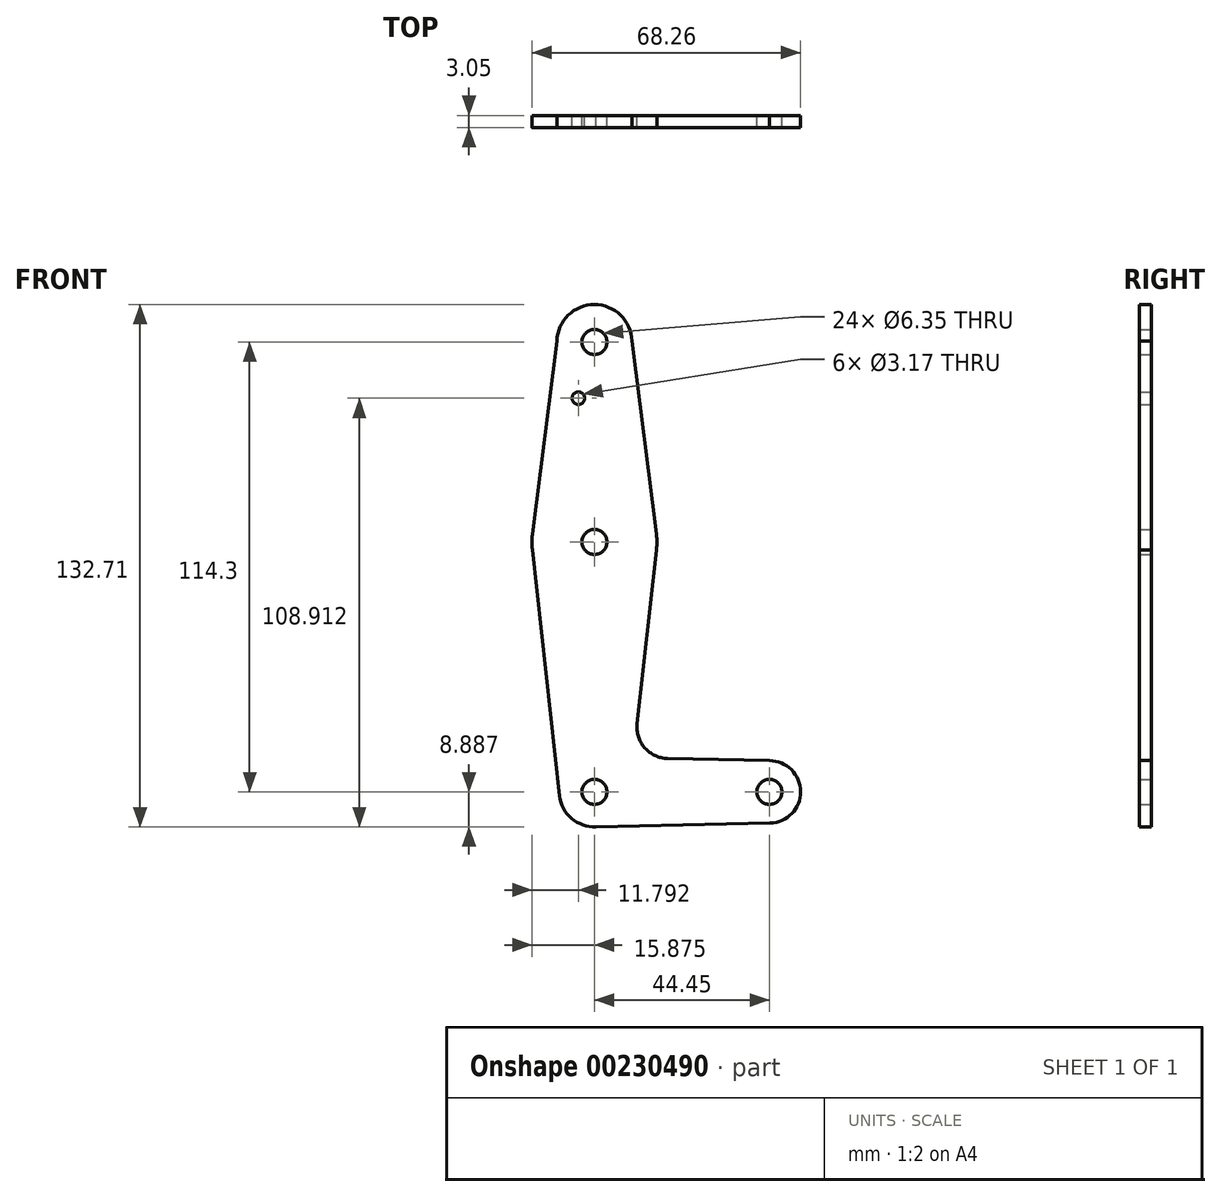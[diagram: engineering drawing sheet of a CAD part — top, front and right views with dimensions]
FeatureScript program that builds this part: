
annotation { "Feature Type Name" : "Feature", "Feature Type Description" : "" }
export const myFeature = defineFeature(function(context is Context, id is Id, definition is map)
    precondition{}
    {
        {
            var Q0;
            Q0=qCreatedBy(makeId("Front.planeOp"),FACE);
            var sketch = newSketch(context, id + "F0", { "sketchPlane" : qUnion([Q0])});
            skLineSegment(sketch, "E0", {"start": v(-39.2, 9.58) * mm, "end": v(-39.2, -53.92) * mm});
            skLineSegment(sketch, "E1", {"start": v(-39.2, -53.92) * mm, "end": v(5.25, -53.92) * mm});
            skCircle(sketch, "E2", {"center": v(-39.2, 60.38) * mm, "radius": 9.53 * mm});
            skCircle(sketch, "E3", {"center": v(-39.2, 9.58) * mm, "radius": 15.88 * mm});
            skCircle(sketch, "E4", {"center": v(-39.2, -53.92) * mm, "radius": 8.89 * mm});
            skLineSegment(sketch, "E5", {"start": v(-39.2, 60.38) * mm, "end": v(-39.2, -53.92) * mm});
            skCircle(sketch, "E6", {"center": v(5.25, -53.92) * mm, "radius": 7.94 * mm});
            skLineSegment(sketch, "E7", {"start": v(-48.73, 60.62) * mm, "end": v(-54.95, 11.58) * mm});
            skLineSegment(sketch, "E8", {"start": v(-29.68, 60.64) * mm, "end": v(-23.46, 11.58) * mm});
            skLineSegment(sketch, "E9", {"start": v(-54.95, 7.58) * mm, "end": v(-48.04, -54.9) * mm});
            skLineSegment(sketch, "E10", {"start": v(-23.46, 7.58) * mm, "end": v(-28.34, -36.6) * mm});
            skLineSegment(sketch, "E11", {"start": v(5.25, -45.99) * mm, "end": v(-20.61, -45.43) * mm});
            skLineSegment(sketch, "E12", {"start": v(-39.2, -62.81) * mm, "end": v(5.42, -61.86) * mm});
            skCircle(sketch, "E13", {"center": v(-39.2, 60.38) * mm, "radius": 3.17 * mm});
            skCircle(sketch, "E14", {"center": v(-39.2, 9.58) * mm, "radius": 3.18 * mm});
            skCircle(sketch, "E15", {"center": v(-43.29, 46.1) * mm, "radius": 1.59 * mm});
            skCircle(sketch, "E16", {"center": v(-39.2, -53.92) * mm, "radius": 3.17 * mm});
            skCircle(sketch, "E17", {"center": v(5.25, -53.92) * mm, "radius": 3.17 * mm});
            skPoint(sketch, "E18.newPointA", {"position": v(-30.37, -54.9) * mm});
            skArc(sketch, "E18.filletArc", {"start": v(-28.34, -36.6) * mm, "mid": v(-26.42, -42.72) * mm, "end": v(-20.61, -45.43) * mm});
            skSolve(sketch);
        }
        {
            var Q0;
            Q0 = qSketchRegion(id + "F0", true);
            var Q1;
            {var subQ0=sQuery(id+"F0.wireOp",EDGE,"E16");var subQ1=sQuery(id+"F0.wireOp",EDGE,"E1");var subQ2=makeQuery(id+"F0.imprint","INTERSECT",VERTEX,{"derivedFrom":[subQ1,subQ0]});Q1=makeQuery(id+"F0.imprint","IMPRINT",FACE,{"disambiguationData":[TD([[makeQuery(id+"F0.imprint","IMPRINT",EDGE,{"disambiguationData":[TD([[subQ2,-1.0]])],"derivedFrom":subQ1}),1.0]])]});}
            extrude(context, id + "F1", {"entities" : qUnion([Q0, Q1]), "depth" : 3.05 * mm});
        }
    });
